# Revit family: MT-TF_SGL HINGE DOOR
name_source: partatom
category: Doors
revit_build: Autodesk Revit 2017 (Build: 20160225_1515(x64)
units: mm (PartAtom-declared; Revit-internal decimal feet)

## family parameters
Always vertical = Yes
Cut with Voids When Loaded = No
Host = Wall
OmniClass Number = 23.30.20.00
OmniClass Title = Windows
Room Calculation Point = No
Shared = No

## types (2) — shared parameters
AIR POCKET = 12 mm  [stored 0.0393701 ft]
ANZRC COMPLIANT = YES
BOT PANEL POSITION = 27 mm  [stored 0.0885827 ft]
DOUBLE GLAZED THICKNESS = 24 mm  [stored 0.0787402 ft]
FRAME MATERIAL = <By Category>
GLAZED MATERIAL = Glass
MAX HEIGHT = 3000 mm
MAX PANEL HEIGHT = 3000 mm
MAX PANEL WIDTH = 3000 mm
MAX WIDTH = 3000 mm
MIDRAIL LENGTH = 112 mm  [stored 0.367454 ft]
Manufacturer = ALSPEC
Model = HAWKESBURY TOP HUNG COMMERCIAL SLIDING DOOR
OFFSET = 10 mm  [stored 0.0328084 ft]
URL = WWW.ALSPEC.COM.AU
VERSION = 2.1
WARNING = No
Wall Closure = By host
YEAR = 2019
zero-valued in all types: Default Sill Height, TOLERANCE

## per-type parameters (varying)
| type | DIMA | Height | OVERALL FRAME HEIGHT | OVERALL FRAME WIDTH | PANEL HEIGHT | PANEL WIDTH | Rough Height | Rough Width | Width |
| ASW100 MITRED ADAPTOR | 750 mm | 1800 mm | 1800 mm | 1500 mm  [stored 4.92126 ft] | 1680 mm | 1371 mm | 1800 mm | 1500 mm  [stored 4.92126 ft] | 1500 mm  [stored 4.92126 ft] |
| TYPICAL | 1000 mm  [stored 3.28084 ft] | 2700 mm  [stored 8.85827 ft] | 2700 mm  [stored 8.85827 ft] | 1200 mm  [stored 3.93701 ft] | 2580 mm  [stored 8.46457 ft] | 1071 mm  [stored 3.51378 ft] | 2700 mm  [stored 8.85827 ft] | 1200 mm  [stored 3.93701 ft] | 1200 mm  [stored 3.93701 ft] |

note: [stored X ft] marks values corroborated as IEEE doubles in the binary element streams (Revit-internal decimal feet)

## geometry (parser evidence)
native form markers: Sweep x17
no freeform markers — native parametric forms only
